# Revit family: 3033942 Lighting Fixture_Sylvania_Insaver HO Topper LED II_Ceiling Recessed
name_source: partatom
category: Lighting Fixtures
revit_build: Autodesk Revit 2017 (Build: 20190507_1515(x64)
units: mm (PartAtom-declared; Revit-internal decimal feet)

## family parameters
Cut with Voids When Loaded = No
Host = Face
Light Source = Yes
OmniClass Number = 23.80.70.11.17
OmniClass Title = Specialized Lighting by Location or Use
Part Type = Normal
Room Calculation Point = No
Round Connector Dimension = Use Diameter
Shared = No

## types (1)
- Insaver HO Topper LED II 205 RO 21W WW
    Accessory Diameter = 220 mm  [stored 0.721785 ft]
    Accessory Marerial = Metallic Paint_Sylvania_Insaver HO Topper LED_White_RAL 9003
    Apparent Load = 21 VA
    Assembly Code = D5020200
    Beam Angle = 74°
    Body Material = Metallic Paint_Sylvania_Insaver HO Topper LED_White_RAL 9003
    CRI ( Ra ) = 80
    Catalog Number = 3033942 Insaver HO Topper LED II 205 RO 21W WW
    Color Filter = 16777215
    Cutout Diameter = 205 mm  [stored 0.672572 ft]
    Default Elevation = 0 mm  [stored 0 ft]
    Description = Insaver HO Topper LED II is available in 4 different round cut out sizes: 150mm, 175mm, 205mm & 220mm Insaver HO Topper LED II 150 12W delivers a 1,134 lumen output (4,000K) - perfect for 1x26W CFL replacement Insaver HO Topper LED II 175 15W delivers a 1,480 lumen output (4,000K) - perfect for 1x32W/2x18W CFL replacement Insaver HO Topper LED II 205 21W delivers a 1,989 lumen output (4,000K) - perfect for 1x42W CFL replacement Insaver HO Topper LED II 225 25W delivers a 2,289 lumen output (4,000K)- perfect for 2x26W CFL replacement High efficacy up to 99lm/W (Insaver HO Topper LED II 175 4,000K) IP44 rating allows for installation in applicable wet zone areas Choice of 3,000K (warm white) or 4,000K (neutral white) Shallow recess depth of <65mm Can replace existing large CFL downlights using a 225mm ceiling cut out (Insaver HO Topper LED II 225) Energy efficient electronic gear including analogue 1-10V and DALI dimmable options IK07 polycarbonate diffuser allows for a wider light distribution than a reflector downlight, allowing for increased spacings between luminaires 3 hour emergency pack available (to be ordered in addition to the luminaire) Ideal for applications such as corridors, public WCs and back of house areas Quick and easy to install Loop in-Loop out facility with red push fit terminal block for quick wiring White bezel (RAL 9003) Energy Class: A++, A+, A Long lifetime: 50,000 hours life at L70 (L80: 30,000 hours, L90: 15,000 hours)
    Diameter = 205 mm  [stored 0.672572 ft]
    Diffuser Diameter = 196 mm  [stored 0.643045 ft]
    Difuser Material = Polycarbonate_Sylvania_Insaver HO Topper LED_3000K
    Dimming Lamp Color Temperature Shift = <None>
    Distribution type = Direct - Symmetrical
    Drive Current = 450 mA
    Electrical Protection = Class II
    Emit Shape Visible in Rendering = Yes
    Emit from Circle Diameter = 196 mm  [stored 0.643045 ft]
    Glow Wire Test = 650 °C
    Height = 60 mm  [stored 0.19685 ft]
    IK Rating = IK07
    IP Rating = IP44
    Inner Diameter = 200 mm  [stored 0.656168 ft]
    Inner Radius = 100 mm  [stored 0.328084 ft]
    LOR = 100 %
    Lamp = 21W
    Lamp Comments = Integrated LED
    Life = 50 000 h
    Manufacturer = Feilo Sylvania
    Model = Insaver HO Topper LED II 205 RO 21W WW
    Photometric Web File = 3033942_InsaverHOTopperLEDII205RO21WWW-194835.ies
    Product Family = INSAVER HO TOPPER LED II
    Product Page URL = http://www.sylvania-lighting.com
    Reflector Material = Metal_Sylvania_Insaver HO Topper LED
    Ta Rating = -10°C to +40°C
    Tilt Angle = -90°
    URL = http://www.sylvania-lighting.com
    Voltage = 230 V
    Voltage Comments = UNV (Universal Voltage; 220-240 Volt)
    Weight = 1 kg

note: [stored X ft] marks values corroborated as IEEE doubles in the binary element streams (Revit-internal decimal feet)

## geometry (parser evidence)
native form markers: Blend x4, Sweep x1
no freeform markers — native parametric forms only
